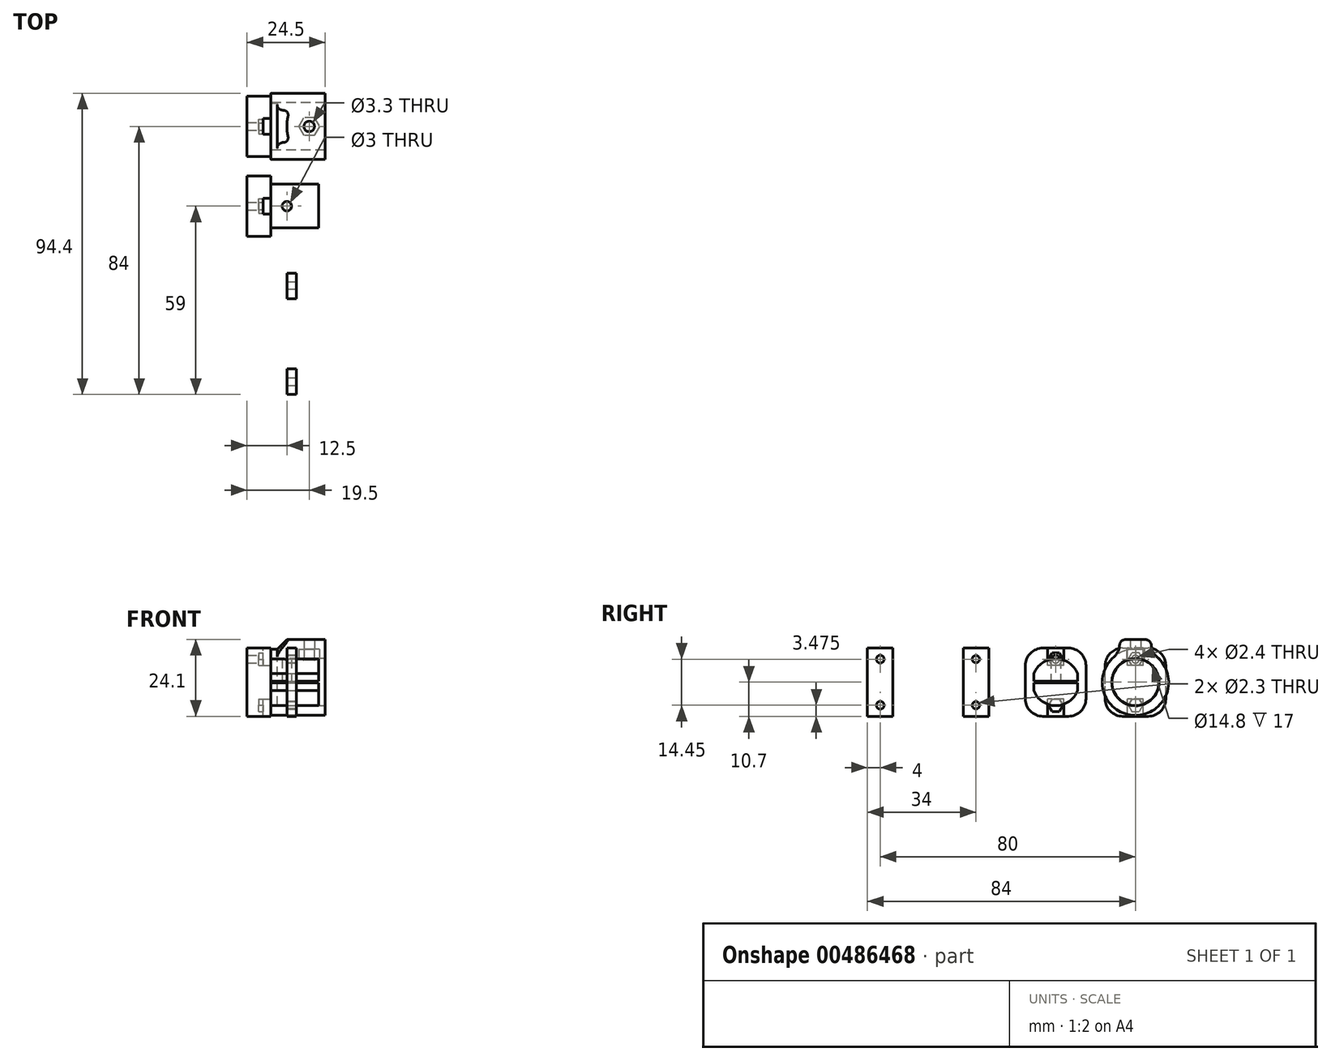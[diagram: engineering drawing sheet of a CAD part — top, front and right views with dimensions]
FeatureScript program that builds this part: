
annotation { "Feature Type Name" : "Feature", "Feature Type Description" : "" }
export const myFeature = defineFeature(function(context is Context, id is Id, definition is map)
    precondition{}
    {
        {
            assignVariable(context, id + "F0", {"name" : "nut_distance", "anyValue" : 5 * mm});
        }
        {
            var Q0;
            Q0=qCreatedBy(makeId("Front.planeOp"),FACE);
            var sketch = newSketch(context, id + "F1", { "sketchPlane" : qUnion([Q0])});
            skLineSegment(sketch, "E0", {"start": v(0, 3.75) * mm, "end": v(-7.5, 3.75) * mm});
            skLineSegment(sketch, "E1", {"start": v(-7.5, -3.75) * mm, "end": v(-7.5, 3.75) * mm});
            skLineSegment(sketch, "E2", {"start": v(-7.5, -3.75) * mm, "end": v(0, -3.75) * mm});
            skLineSegment(sketch, "E3", {"start": v(0, -10.7) * mm, "end": v(0, -3.75) * mm});
            skLineSegment(sketch, "E4", {"start": v(0, -10.7) * mm, "end": v(-12.5, -10.7) * mm});
            skLineSegment(sketch, "E5", {"start": v(-12.5, -10.7) * mm, "end": v(-12.5, 10.7) * mm});
            skLineSegment(sketch, "E6", {"start": v(0, 3.75) * mm, "end": v(0, 10.7) * mm});
            skLineSegment(sketch, "E7", {"start": v(-12.5, 10.7) * mm, "end": v(0, 10.7) * mm});
            skSolve(sketch);
        }
        {
            var Q0;
            Q0=qSketchRegion(id+"F1",true);
            extrude(context, id + "F2", {"entities" : qUnion([Q0]), "depth" : 8 * mm, "offsetDistance" : 25 * mm, "symmetric" : true});
        }
        {
            var Q0;
            Q0=makeQuery(id+"F2.opExtrude","SWEPT_FACE",FACE,{"disambiguationData":[OSD([sQuery(id+"F1.wireOp",EDGE,"E6")])]});
            var sketch = newSketch(context, id + "F3", { "sketchPlane" : qUnion([Q0])});
            skLineSegment(sketch, "E8", {"start": v(-12.42, 0) * mm, "end": v(17.97, 0) * mm, "construction": true});
            skLineSegment(sketch, "E9", {"start": v(0, 22.03) * mm, "end": v(0, -15.29) * mm, "construction": true});
            skPoint(sketch, "E9.startSnap0", {"position": v(0, 10.7) * mm});
            skLineSegment(sketch, "E10", {"start": v(0, 5.25) * mm, "end": v(-1.14, 5.25) * mm});
            skLineSegment(sketch, "E11", {"start": v(-1.14, 5.25) * mm, "end": v(-2.28, 7.22) * mm});
            skLineSegment(sketch, "E12", {"start": v(-2.28, 7.22) * mm, "end": v(0, 7.22) * mm, "construction": true});
            skLineSegment(sketch, "E13", {"start": v(0, 7.22) * mm, "end": v(1.14, 5.25) * mm, "construction": true});
            skLineSegment(sketch, "E14.MirrorCS", {"start": v(-1.14, 9.2) * mm, "end": v(-2.28, 7.22) * mm});
            skLineSegment(sketch, "E15.MirrorCS", {"start": v(0, 9.2) * mm, "end": v(-1.14, 9.2) * mm});
            skLineSegment(sketch, "E16.MirrorCS", {"start": v(0, 9.2) * mm, "end": v(1.14, 9.2) * mm});
            skLineSegment(sketch, "E17.MirrorCS", {"start": v(1.14, 9.2) * mm, "end": v(2.28, 7.23) * mm});
            skLineSegment(sketch, "E18.MirrorCS", {"start": v(1.14, 5.25) * mm, "end": v(2.28, 7.23) * mm});
            skLineSegment(sketch, "E19.MirrorCS", {"start": v(0, 5.25) * mm, "end": v(1.14, 5.25) * mm});
            skLineSegment(sketch, "E20.MirrorCS", {"start": v(-1.14, -9.2) * mm, "end": v(-2.28, -7.22) * mm});
            skLineSegment(sketch, "E21.MirrorCS", {"start": v(0, -9.2) * mm, "end": v(-1.14, -9.2) * mm});
            skLineSegment(sketch, "E22.MirrorCS", {"start": v(0, -9.2) * mm, "end": v(1.14, -9.2) * mm});
            skLineSegment(sketch, "E23.MirrorCS", {"start": v(1.14, -9.2) * mm, "end": v(2.28, -7.23) * mm});
            skLineSegment(sketch, "E24.MirrorCS", {"start": v(1.14, -5.25) * mm, "end": v(2.28, -7.23) * mm});
            skLineSegment(sketch, "E25.MirrorCS", {"start": v(0, -5.25) * mm, "end": v(1.14, -5.25) * mm});
            skLineSegment(sketch, "E26.MirrorCS", {"start": v(0, -5.25) * mm, "end": v(-1.14, -5.25) * mm});
            skLineSegment(sketch, "E27.MirrorCS", {"start": v(-1.14, -5.25) * mm, "end": v(-2.28, -7.23) * mm});
            skSolve(sketch);
        }
        {
            var Q0;
            Q0=makeQuery(id+"F3.imprint","IMPRINT",FACE,{"disambiguationData":[TD([[makeQuery(id+"F3.imprint","IMPRINT",EDGE,{"derivedFrom":sQuery(id+"F3.wireOp",EDGE,"E10")}),-1.0]])]});
            var Q1;
            Q1=makeQuery(id+"F3.imprint","IMPRINT",FACE,{"disambiguationData":[TD([[makeQuery(id+"F3.imprint","IMPRINT",EDGE,{"derivedFrom":sQuery(id+"F3.wireOp",EDGE,"E20.MirrorCS")}),-1.0]])]});
            extrude(context, id + "F4", {"entities" : qUnion([Q0, Q1]), "operationType" : NewBodyOperationType.REMOVE, "oppositeDirection" : true, "depth" : 5.4 * mm, "hasOffset" : true, "offsetDistance" : 4 * mm, "hasSecondDirection" : true, "secondDirectionOppositeDirection" : true, "secondDirectionDepth" : getVariable(context, 'nut_distance') - 1.3 * mm});
        }
        {
            var Q0;
            Q0=makeQuery(id+"F2.opExtrude","SWEPT_FACE",FACE,{"disambiguationData":[OSD([sQuery(id+"F1.wireOp",EDGE,"E7")])]});
            var sketch = newSketch(context, id + "F5", { "sketchPlane" : qUnion([Q0])});
            skLineSegment(sketch, "E28.bottom", {"start": v(-7.5, 2.5) * mm, "end": v(-5, 2.5) * mm});
            skLineSegment(sketch, "E28.top", {"start": v(-7.5, -2.5) * mm, "end": v(-5, -2.5) * mm});
            skLineSegment(sketch, "E28.left", {"start": v(-7.5, 2.5) * mm, "end": v(-7.5, -2.5) * mm});
            skLineSegment(sketch, "E28.right", {"start": v(-5, 2.5) * mm, "end": v(-5, -2.5) * mm});
            skSolve(sketch);
        }
        {
            var Q0;
            Q0=qSketchRegion(id+"F5",true);
            var Q1;
            Q1=makeQuery(id+"F4.boolean.opBoolean","COPY",VERTEX,{"derivedFrom":makeQuery(id+"F4.opExtrude","CAP_VERTEX",VERTEX,{"disambiguationData":[OSD([sQuery(id+"F3.wireOp",EDGE,"E10"),sQuery(id+"F3.wireOp",EDGE,"E11")])],"isStart":false})});
            extrude(context, id + "F6", {"entities" : qUnion([Q0]), "operationType" : NewBodyOperationType.REMOVE, "endBound" : BoundingType.UP_TO_VERTEX, "oppositeDirection" : true, "depth" : 25 * mm, "endBoundEntityVertex" : qUnion([Q1]), "offsetDistance" : 25 * mm});
        }
        {
            var Q0;
            Q0=makeQuery(id+"F2.opExtrude","SWEPT_FACE",FACE,{"disambiguationData":[OSD([sQuery(id+"F1.wireOp",EDGE,"E6")])]});
            var sketch = newSketch(context, id + "F7", { "sketchPlane" : qUnion([Q0])});
            skCircle(sketch, "E29", {"center": v(0, 7.22) * mm, "radius": 1.2 * mm});
            skCircle(sketch, "E30.MirrorC", {"center": v(0, -7.22) * mm, "radius": 1.2 * mm});
            skSolve(sketch);
        }
        {
            var Q0;
            Q0=makeQuery(id+"F7.imprint","IMPRINT",FACE,{"disambiguationData":[TD([[makeQuery(id+"F7.imprint","IMPRINT",EDGE,{"derivedFrom":sQuery(id+"F7.wireOp",EDGE,"E29")}),1.0]])]});
            var Q1;
            Q1=makeQuery(id+"F7.imprint","IMPRINT",FACE,{"disambiguationData":[TD([[makeQuery(id+"F7.imprint","IMPRINT",EDGE,{"derivedFrom":sQuery(id+"F7.wireOp",EDGE,"E30.MirrorC")}),-1.0]])]});
            var Q2;
            Q2=makeQuery(id+"F4.boolean.opBoolean","COPY",VERTEX,{"derivedFrom":makeQuery(id+"F4.opExtrude","CAP_VERTEX",VERTEX,{"disambiguationData":[OSD([sQuery(id+"F3.wireOp",EDGE,"E17.MirrorCS"),sQuery(id+"F3.wireOp",EDGE,"E18.MirrorCS")])],"isStart":false})});
            extrude(context, id + "F8", {"entities" : qUnion([Q0, Q1]), "operationType" : NewBodyOperationType.REMOVE, "endBound" : BoundingType.THROUGH_ALL, "oppositeDirection" : true, "depth" : 25 * mm, "endBoundEntityVertex" : qUnion([Q2]), "offsetDistance" : 25 * mm});
        }
        {
            var Q0;
            Q0=qSketchRegion(id+"F5",true);
            var Q1;
            Q1=makeQuery(id+"F2.opExtrude","SWEPT_FACE",FACE,{"disambiguationData":[OSD([sQuery(id+"F1.wireOp",EDGE,"E4")])]});
            var Q2;
            Q2=makeQuery(id+"F4.boolean.opBoolean","COPY",VERTEX,{"derivedFrom":makeQuery(id+"F4.opExtrude","CAP_VERTEX",VERTEX,{"disambiguationData":[OSD([sQuery(id+"F3.wireOp",EDGE,"E26.MirrorCS"),sQuery(id+"F3.wireOp",EDGE,"E27.MirrorCS")])],"isStart":false})});
            extrude(context, id + "F9", {"entities" : qUnion([Q0]), "operationType" : NewBodyOperationType.REMOVE, "endBound" : BoundingType.UP_TO_SURFACE, "oppositeDirection" : true, "depth" : 25 * mm, "endBoundEntityFace" : qUnion([Q1]), "offsetDistance" : 25 * mm, "hasSecondDirection" : true, "secondDirectionBound" : BoundingType.UP_TO_VERTEX, "secondDirectionOppositeDirection" : true, "secondDirectionDepth" : 25 * mm, "secondDirectionBoundEntityVertex" : qUnion([Q2])});
        }
        {
            var Q0;
            Q0=qSketchRegion(id+"F3",true);
            extrude(context, id + "F10", {"entities" : qUnion([Q0]), "operationType" : NewBodyOperationType.REMOVE, "oppositeDirection" : true, "depth" : (7.5 + 1.3) * mm, "offsetDistance" : 25 * mm, "hasSecondDirection" : true, "secondDirectionOppositeDirection" : true, "secondDirectionDepth" : (5.4 + 1.7) * mm});
        }
        {
            var Q0;
            Q0=qCreatedBy(makeId("Front.planeOp"),FACE);
            cPlane(context, id + "F11", {"entities" : qUnion([Q0]), "cplaneType" : CPlaneType.OFFSET, "offset" : 25 * mm, "width" : 150 * mm, "height" : 150 * mm});
        }
        {
            var Q0;
            Q0=qCreatedBy(makeId("Right.planeOp"),FACE);
            var sketch = newSketch(context, id + "F12", { "sketchPlane" : qUnion([Q0])});
            skLineSegment(sketch, "E31.bottom", {"start": v(-21, 10.7) * mm, "end": v(-29, 10.7) * mm});
            skLineSegment(sketch, "E31.top", {"start": v(-21, -10.7) * mm, "end": v(-29, -10.7) * mm});
            skLineSegment(sketch, "E31.left", {"start": v(-21, 10.7) * mm, "end": v(-21, -10.7) * mm});
            skLineSegment(sketch, "E31.right", {"start": v(-29, 10.7) * mm, "end": v(-29, -10.7) * mm});
            skCircle(sketch, "E32", {"center": v(-25, 7.22) * mm, "radius": 1.15 * mm});
            skCircle(sketch, "E33.MirrorC", {"center": v(-25, -7.22) * mm, "radius": 1.15 * mm});
            skSolve(sketch);
        }
        {
            var Q0;
            Q0=makeQuery(id+"F12.imprint","IMPRINT",FACE,{"disambiguationData":[TD([[makeQuery(id+"F12.imprint","IMPRINT",EDGE,{"derivedFrom":sQuery(id+"F12.wireOp",EDGE,"E31.bottom")}),1.0]])]});
            extrude(context, id + "F13", {"entities" : qUnion([Q0]), "depth" : 3 * mm, "offsetDistance" : 25 * mm});
        }
        {
            var Q0;
            Q0=qCreatedBy(id+"F11.planeOp",FACE);
            var sketch = newSketch(context, id + "F14", { "sketchPlane" : qUnion([Q0])});
            skArc(sketch, "E34", {"start": v(0, 3.75) * mm, "mid": v(-0.1, 0) * mm, "end": v(0, -3.75) * mm});
            skLineSegment(sketch, "E35", {"start": v(0, 3.75) * mm, "end": v(0, -3.75) * mm});
            skSolve(sketch);
        }
        {
            var Q0;
            Q0=makeQuery(id+"F13.opExtrude","SWEPT_BODY",BODY,{"disambiguationData":[OSD([sQuery(id+"F12.wireOp",EDGE,"E31.bottom"),sQuery(id+"F12.wireOp",EDGE,"E31.top"),sQuery(id+"F12.wireOp",EDGE,"E31.left"),sQuery(id+"F12.wireOp",EDGE,"E31.right"),sQuery(id+"F12.wireOp",EDGE,"E32"),sQuery(id+"F12.wireOp",EDGE,"E33.MirrorC")])]});
            transform(context, id + "F15", {"entities" : qUnion([Q0]), "transformType" : TransformType.TRANSLATION_3D, "dx" : 0 * mm, "dy" : -30 * mm, "dz" : 0 * mm, "makeCopy" : true});
        }
        {
            var Q0;
            Q0=makeQuery(id+"F15.opPattern","COPY",FACE,{"derivedFrom":makeQuery(id+"F13.opExtrude","CAP_FACE",FACE,{"disambiguationData":[OSD([sQuery(id+"F12.wireOp",EDGE,"E31.bottom"),sQuery(id+"F12.wireOp",EDGE,"E31.top"),sQuery(id+"F12.wireOp",EDGE,"E31.left"),sQuery(id+"F12.wireOp",EDGE,"E31.right"),sQuery(id+"F12.wireOp",EDGE,"E32"),sQuery(id+"F12.wireOp",EDGE,"E33.MirrorC")])],"isStart":false}),"instanceName":"1"});
            var sketch = newSketch(context, id + "F16", { "sketchPlane" : qUnion([Q0])});
            skCircle(sketch, "E36", {"center": v(-55, 7.22) * mm, "radius": 1.2 * mm});
            skCircle(sketch, "E37.MirrorC", {"center": v(-55, -7.22) * mm, "radius": 1.2 * mm});
            skSolve(sketch);
        }
        {
            var Q0;
            Q0=qSketchRegion(id+"F16",true);
            extrude(context, id + "F17", {"entities" : qUnion([Q0]), "operationType" : NewBodyOperationType.REMOVE, "endBound" : BoundingType.THROUGH_ALL, "oppositeDirection" : true, "depth" : 25 * mm, "offsetDistance" : 25 * mm});
        }
        {
            var Q0;
            Q0=qCreatedBy(makeId("Right.planeOp"),FACE);
            var sketch = newSketch(context, id + "F18", { "sketchPlane" : qUnion([Q0])});
            skCircle(sketch, "E38", {"center": v(0, 0) * mm, "radius": 7.35 * mm});
            skSolve(sketch);
        }
        {
            var Q0;
            Q0=makeQuery(id+"F2.opExtrude","SWEPT_FACE",FACE,{"disambiguationData":[OSD([sQuery(id+"F1.wireOp",EDGE,"E1")])]});
            var sketch = newSketch(context, id + "F19", { "sketchPlane" : qUnion([Q0])});
            skLineSegment(sketch, "E39.bottom", {"start": v(4, 3.75) * mm, "end": v(-4, 3.75) * mm});
            skLineSegment(sketch, "E39.top", {"start": v(4, -3.75) * mm, "end": v(-4, -3.75) * mm});
            skLineSegment(sketch, "E39.left", {"start": v(4, 3.75) * mm, "end": v(4, -3.75) * mm});
            skLineSegment(sketch, "E39.right", {"start": v(-4, 3.75) * mm, "end": v(-4, -3.75) * mm});
            skSolve(sketch);
        }
        {
            var Q0;
            Q0 = qSketchRegion(id + "F19", true);
            var Q1;
            Q1=makeQuery(id+"F2.opExtrude","SWEPT_FACE",FACE,{"disambiguationData":[OSD([sQuery(id+"F1.wireOp",EDGE,"E6")])]});
            extrude(context, id + "F20", {"entities" : qUnion([Q0]), "operationType" : NewBodyOperationType.ADD, "endBound" : BoundingType.UP_TO_SURFACE, "depth" : 25 * mm, "endBoundEntityFace" : qUnion([Q1]), "offsetDistance" : 25 * mm});
        }
        {
            var Q0;
            Q0 = qSketchRegion(id + "F18", true);
            extrude(context, id + "F21", {"entities" : qUnion([Q0]), "operationType" : NewBodyOperationType.ADD, "oppositeDirection" : true, "depth" : 5 * mm, "offsetDistance" : 25 * mm, "hasSecondDirection" : true, "secondDirectionOppositeDirection" : false, "secondDirectionDepth" : 10 * mm});
        }
        {
            var Q0;
            {var subQ0=sQuery(id+"F1.wireOp",EDGE,"E7");var subQ1=sQuery(id+"F1.wireOp",EDGE,"E6");var subQ4=sQuery(id+"F1.wireOp",EDGE,"E3");var subQ8=makeQuery(id+"F2.opExtrude","SWEPT_FACE",FACE,{"disambiguationData":[OSD([subQ1])]});var subQ9=sQuery(id+"F19.wireOp",EDGE,"E39.left");var subQ10=sQuery(id+"F19.wireOp",EDGE,"E39.right");Q0=makeQuery(id+"F21.boolean.opBoolean","SPLIT",FACE,{"disambiguationData":[TD([makeQuery(id+"F2.opExtrude","SWEPT_FACE",FACE,{"disambiguationData":[OSD([subQ0])]})])],"derivedFrom":makeQuery(id+"F20.boolean.opBoolean","MERGE",FACE,{"derivedFrom":[makeQuery(id+"F2.opExtrude","SWEPT_FACE",FACE,{"disambiguationData":[OSD([subQ4])]}),subQ8,makeQuery(id+"F20.opExtrude","CAP_FACE",FACE,{"disambiguationData":[OSD([sQuery(id+"F19.wireOp",EDGE,"E39.bottom"),sQuery(id+"F19.wireOp",EDGE,"E39.top"),subQ9,subQ10])],"isStart":false})]})});}
            var sketch = newSketch(context, id + "F22", { "sketchPlane" : qUnion([Q0])});
            skArc(sketch, "E40", {"start": v(4, 6.17) * mm, "mid": v(0, 7.35) * mm, "end": v(-4, 6.17) * mm});
            skLineSegment(sketch, "E41", {"start": v(-4, 6.17) * mm, "end": v(-4, 10.7) * mm});
            skLineSegment(sketch, "E42", {"start": v(-4, 10.7) * mm, "end": v(4, 10.7) * mm});
            skLineSegment(sketch, "E43", {"start": v(4, 10.7) * mm, "end": v(4, 6.17) * mm});
            skArc(sketch, "E44.MirrorCS", {"start": v(4, -6.17) * mm, "mid": v(0, -7.35) * mm, "end": v(-4, -6.17) * mm});
            skLineSegment(sketch, "E45.MirrorCS", {"start": v(-4, -10.7) * mm, "end": v(4, -10.7) * mm});
            skLineSegment(sketch, "E46.MirrorCS", {"start": v(-4, -6.17) * mm, "end": v(-4, -10.7) * mm});
            skLineSegment(sketch, "E47.MirrorCS", {"start": v(4, -10.7) * mm, "end": v(4, -6.17) * mm});
            skSolve(sketch);
        }
        {
            var Q0;
            Q0 = qSketchRegion(id + "F22", true);
            extrude(context, id + "F23", {"entities" : qUnion([Q0]), "operationType" : NewBodyOperationType.REMOVE, "oppositeDirection" : true, "depth" : 5 * mm, "offsetDistance" : 25 * mm});
        }
        {
            var Q0;
            Q0=makeQuery(id+"F2.opExtrude","SWEPT_FACE",FACE,{"disambiguationData":[OSD([sQuery(id+"F1.wireOp",EDGE,"E5")])]});
            var sketch = newSketch(context, id + "F24", { "sketchPlane" : qUnion([Q0])});
            skPoint(sketch, "E48", {"position": v(4, -10.7) * mm});
            skPoint(sketch, "E49", {"position": v(4, 10.7) * mm});
            skLineSegment(sketch, "E50.bottom", {"start": v(9.5, -10.7) * mm, "end": v(4, -10.7) * mm});
            skLineSegment(sketch, "E50.top", {"start": v(9.5, 10.7) * mm, "end": v(4, 10.7) * mm});
            skLineSegment(sketch, "E50.left", {"start": v(9.5, -10.7) * mm, "end": v(9.5, 10.7) * mm});
            skLineSegment(sketch, "E50.right", {"start": v(4, -10.7) * mm, "end": v(4, 10.7) * mm});
            skPoint(sketch, "E51.MirrorP", {"position": v(-4, 10.7) * mm});
            skPoint(sketch, "E52.MirrorP", {"position": v(-4, -10.7) * mm});
            skLineSegment(sketch, "E53.MirrorCS", {"start": v(-9.5, -10.7) * mm, "end": v(-4, -10.7) * mm});
            skLineSegment(sketch, "E54.MirrorCS", {"start": v(-4, -10.7) * mm, "end": v(-4, 10.7) * mm});
            skLineSegment(sketch, "E55.MirrorCS", {"start": v(-9.5, -10.7) * mm, "end": v(-9.5, 10.7) * mm});
            skLineSegment(sketch, "E56.MirrorCS", {"start": v(-9.5, 10.7) * mm, "end": v(-4, 10.7) * mm});
            skSolve(sketch);
        }
        {
            var Q0;
            Q0 = qSketchRegion(id + "F24", true);
            var Q1;
            {var subQ0=sQuery(id+"F18.wireOp",EDGE,"E38");Q1=makeQuery(id+"F21.boolean.opBoolean","SPLIT",FACE,{"disambiguationData":[TD([makeQuery(id+"F20.opExtrude","SWEPT_FACE",FACE,{"disambiguationData":[OSD([sQuery(id+"F19.wireOp",EDGE,"E39.right")])]})])],"derivedFrom":makeQuery(id+"F21.opExtrude","CAP_FACE",FACE,{"disambiguationData":[OSD([subQ0])],"isStart":false})});}
            extrude(context, id + "F25", {"entities" : qUnion([Q0]), "operationType" : NewBodyOperationType.ADD, "endBound" : BoundingType.UP_TO_SURFACE, "oppositeDirection" : true, "depth" : 5 * mm, "endBoundEntityFace" : qUnion([Q1]), "offsetDistance" : 25 * mm});
        }
        {
            var Q0;
            Q0=makeQuery(id+"F25.opExtrude","SWEPT_EDGE",EDGE,{"disambiguationData":[OSD([sQuery(id+"F24.wireOp",EDGE,"E50.top"),sQuery(id+"F24.wireOp",EDGE,"E50.left")])]});
            var Q1;
            Q1=makeQuery(id+"F25.opExtrude","SWEPT_EDGE",EDGE,{"disambiguationData":[OSD([sQuery(id+"F24.wireOp",EDGE,"E55.MirrorCS"),sQuery(id+"F24.wireOp",EDGE,"E56.MirrorCS")])]});
            var Q2;
            Q2=makeQuery(id+"F25.opExtrude","SWEPT_EDGE",EDGE,{"disambiguationData":[OSD([sQuery(id+"F24.wireOp",EDGE,"E53.MirrorCS"),sQuery(id+"F24.wireOp",EDGE,"E55.MirrorCS")])]});
            var Q3;
            Q3=makeQuery(id+"F25.opExtrude","SWEPT_EDGE",EDGE,{"disambiguationData":[OSD([sQuery(id+"F24.wireOp",EDGE,"E50.bottom"),sQuery(id+"F24.wireOp",EDGE,"E50.left")])]});
            fillet(context, id + "F26", {"entities" : qUnion([Q0, Q1, Q2, Q3]), "radius" : 5.5 * mm, "tangentPropagation" : true, "allowEdgeOverflow" : false});
        }
        {
            var Q0;
            Q0=qCreatedBy(makeId("Top.planeOp"),FACE);
            var sketch = newSketch(context, id + "F27", { "sketchPlane" : qUnion([Q0])});
            skCircle(sketch, "E57", {"center": v(0, 0) * mm, "radius": 1.5 * mm});
            skSolve(sketch);
        }
        {
            var Q0;
            Q0 = qSketchRegion(id + "F27", true);
            extrude(context, id + "F28", {"entities" : qUnion([Q0]), "operationType" : NewBodyOperationType.REMOVE, "depth" : 25 * mm, "offsetDistance" : 25 * mm, "hasSecondDirection" : true, "secondDirectionOppositeDirection" : false, "secondDirectionDepth" : 0 * mm});
        }
        {
            var Q0;
            Q0=qCreatedBy(makeId("Front.planeOp"),FACE);
            cPlane(context, id + "F29", {"entities" : qUnion([Q0]), "cplaneType" : CPlaneType.OFFSET, "offset" : 25 * mm, "oppositeDirection" : true, "width" : 150 * mm, "height" : 150 * mm});
        }
        {
            var Q0;
            Q0=makeQuery(id+"F2.opExtrude","SWEPT_BODY",BODY,{"disambiguationData":[OSD([sQuery(id+"F1.wireOp",EDGE,"E0"),sQuery(id+"F1.wireOp",EDGE,"E1"),sQuery(id+"F1.wireOp",EDGE,"E2"),sQuery(id+"F1.wireOp",EDGE,"E3"),sQuery(id+"F1.wireOp",EDGE,"E4"),sQuery(id+"F1.wireOp",EDGE,"E5"),sQuery(id+"F1.wireOp",EDGE,"E6"),sQuery(id+"F1.wireOp",EDGE,"E7")])]});
            transform(context, id + "F30", {"entities" : qUnion([Q0]), "transformType" : TransformType.TRANSLATION_3D, "dx" : 0 * mm, "dy" : 25 * mm, "dz" : 0 * mm, "makeCopy" : true});
        }
        {
            var Q0;
            Q0=qCreatedBy(makeId("Right.planeOp"),FACE);
            var sketch = newSketch(context, id + "F31", { "sketchPlane" : qUnion([Q0])});
            skCircle(sketch, "E58", {"center": v(25, 0) * mm, "radius": 7.35 * mm});
            skSolve(sketch);
        }
        {
            var Q0;
            Q0=qCreatedBy(makeId("Right.planeOp"),FACE);
            var sketch = newSketch(context, id + "F32", { "sketchPlane" : qUnion([Q0])});
            skCircle(sketch, "E59", {"center": v(25, 0) * mm, "radius": 7.4 * mm});
            skCircle(sketch, "E60", {"center": v(25, 0) * mm, "radius": 10.4 * mm});
            skSolve(sketch);
        }
        {
            var Q0;
            Q0 = qSketchRegion(id + "F32", true);
            extrude(context, id + "F33", {"entities" : qUnion([Q0]), "operationType" : NewBodyOperationType.ADD, "depth" : 12 * mm, "offsetDistance" : 25 * mm, "hasSecondDirection" : true, "secondDirectionOppositeDirection" : true, "secondDirectionDepth" : 5 * mm});
        }
        {
            var Q0;
            Q0 = qSketchRegion(id + "F31", true);
            extrude(context, id + "F34", {"entities" : qUnion([Q0]), "operationType" : NewBodyOperationType.REMOVE, "oppositeDirection" : true, "depth" : 3 * mm, "offsetDistance" : 25 * mm, "hasSecondDirection" : true, "secondDirectionOppositeDirection" : false, "secondDirectionDepth" : 10 * mm});
        }
        {
            var Q0;
            Q0=qCreatedBy(makeId("Top.planeOp"),FACE);
            cPlane(context, id + "F35", {"entities" : qUnion([Q0]), "cplaneType" : CPlaneType.OFFSET, "offset" : (14.8 / 2) * mm, "width" : 150 * mm, "height" : 150 * mm});
        }
        {
            var Q0;
            Q0=qCreatedBy(id+"F35.planeOp",FACE);
            var sketch = newSketch(context, id + "F36", { "sketchPlane" : qUnion([Q0])});
            skCircle(sketch, "E61.cCircle", {"center": v(7, 25) * mm, "radius": 2.8 * mm, "construction": true});
            skLineSegment(sketch, "E61.0", {"start": v(5.38, 27.8) * mm, "end": v(8.62, 27.8) * mm});
            skLineSegment(sketch, "E61.1", {"start": v(8.62, 27.8) * mm, "end": v(10.23, 25) * mm});
            skLineSegment(sketch, "E61.2", {"start": v(10.23, 25) * mm, "end": v(8.62, 22.2) * mm});
            skLineSegment(sketch, "E61.3", {"start": v(8.62, 22.2) * mm, "end": v(5.38, 22.2) * mm});
            skLineSegment(sketch, "E61.4", {"start": v(5.38, 22.2) * mm, "end": v(3.77, 25) * mm});
            skLineSegment(sketch, "E61.5", {"start": v(3.77, 25) * mm, "end": v(5.38, 27.8) * mm});
            skPoint(sketch, "E61.0.midPoint", {"position": v(7, 27.8) * mm});
            skSolve(sketch);
        }
        {
            var Q0;
            Q0=makeQuery(id+"F36.imprint","IMPRINT",FACE,{"disambiguationData":[TD([[makeQuery(id+"F36.imprint","IMPRINT",EDGE,{"derivedFrom":sQuery(id+"F36.wireOp",EDGE,"E61.0")}),-1.0]])]});
            var sketch = newSketch(context, id + "F37", { "sketchPlane" : qUnion([Q0])});
            skLineSegment(sketch, "E62.bottom", {"start": v(12, 20) * mm, "end": v(2, 20) * mm});
            skLineSegment(sketch, "E62.top", {"start": v(12, 30) * mm, "end": v(2, 30) * mm});
            skLineSegment(sketch, "E62.left", {"start": v(12, 20) * mm, "end": v(12, 30) * mm});
            skLineSegment(sketch, "E62.right", {"start": v(2, 20) * mm, "end": v(2, 30) * mm});
            skSolve(sketch);
        }
        {
            var Q0;
            Q0 = qSketchRegion(id + "F37", true);
            extrude(context, id + "F38", {"entities" : qUnion([Q0]), "operationType" : NewBodyOperationType.ADD, "depth" : 6 * mm, "offsetDistance" : 25 * mm});
        }
        {
            var Q0;
            Q0 = qSketchRegion(id + "F36", true);
            extrude(context, id + "F39", {"entities" : qUnion([Q0]), "operationType" : NewBodyOperationType.REMOVE, "depth" : 3 * mm, "offsetDistance" : 25 * mm, "hasSecondDirection" : true, "secondDirectionOppositeDirection" : true, "secondDirectionDepth" : 5 * mm});
        }
        {
            var Q0;
            Q0=qCreatedBy(id+"F35.planeOp",FACE);
            var sketch = newSketch(context, id + "F40", { "sketchPlane" : qUnion([Q0])});
            skCircle(sketch, "E63", {"center": v(7, 25) * mm, "radius": 1.65 * mm});
            skSolve(sketch);
        }
        {
            var Q0;
            Q0 = qSketchRegion(id + "F40", true);
            var Q1;
            Q1=makeQuery(id+"F38.opExtrude","CAP_FACE",FACE,{"disambiguationData":[OSD([sQuery(id+"F37.wireOp",EDGE,"E62.bottom"),sQuery(id+"F37.wireOp",EDGE,"E62.top"),sQuery(id+"F37.wireOp",EDGE,"E62.left"),sQuery(id+"F37.wireOp",EDGE,"E62.right")])],"isStart":false});
            extrude(context, id + "F41", {"entities" : qUnion([Q0]), "operationType" : NewBodyOperationType.REMOVE, "endBound" : BoundingType.UP_TO_SURFACE, "depth" : 25 * mm, "endBoundEntityFace" : qUnion([Q1]), "offsetDistance" : 25 * mm});
        }
        {
            var Q0;
            Q0=makeQuery(id+"F38.boolean.opBoolean","INTERSECT",EDGE,{"derivedFrom":[makeQuery(id+"F33.opExtrude","SWEPT_FACE",FACE,{"disambiguationData":[OSD([sQuery(id+"F32.wireOp",EDGE,"E60")])]}),makeQuery(id+"F38.opExtrude","SWEPT_FACE",FACE,{"disambiguationData":[OSD([sQuery(id+"F37.wireOp",EDGE,"E62.right")])]})]});
            chamfer(context, id + "F42", {"entities" : qUnion([Q0]), "chamferType" : ChamferType.OFFSET_ANGLE, "width" : 5 * mm, "oppositeDirection" : false, "angle" : 45 * degree, "tangentPropagation" : true});
        }
        {
            var Q0;
            Q0=makeQuery(id+"F38.opExtrude","CAP_EDGE",EDGE,{"disambiguationData":[OSD([sQuery(id+"F37.wireOp",EDGE,"E62.top")])],"isStart":false});
            var Q1;
            Q1=makeQuery(id+"F38.opExtrude","CAP_EDGE",EDGE,{"disambiguationData":[OSD([sQuery(id+"F37.wireOp",EDGE,"E62.bottom")])],"isStart":false});
            fillet(context, id + "F43", {"entities" : qUnion([Q0, Q1]), "radius" : 2 * mm, "tangentPropagation" : true, "allowEdgeOverflow" : false});
        }
        {
            var Q0;
            Q0=makeQuery(id+"F38.boolean.opBoolean","INTERSECT",EDGE,{"derivedFrom":[makeQuery(id+"F33.opExtrude","SWEPT_FACE",FACE,{"disambiguationData":[OSD([sQuery(id+"F32.wireOp",EDGE,"E60")])]}),makeQuery(id+"F38.opExtrude","SWEPT_FACE",FACE,{"disambiguationData":[OSD([sQuery(id+"F37.wireOp",EDGE,"E62.top")])]})]});
            var Q1;
            Q1=makeQuery(id+"F38.boolean.opBoolean","INTERSECT",EDGE,{"derivedFrom":[makeQuery(id+"F33.opExtrude","SWEPT_FACE",FACE,{"disambiguationData":[OSD([sQuery(id+"F32.wireOp",EDGE,"E60")])]}),makeQuery(id+"F38.opExtrude","SWEPT_FACE",FACE,{"disambiguationData":[OSD([sQuery(id+"F37.wireOp",EDGE,"E62.bottom")])]})]});
            fillet(context, id + "F44", {"entities" : qUnion([Q0, Q1]), "radius" : 5 * mm, "tangentPropagation" : true, "allowEdgeOverflow" : false});
        }
        {
            var Q0;
            Q0=makeQuery(id+"F21.opExtrude","CAP_FACE",FACE,{"disambiguationData":[OSD([sQuery(id+"F18.wireOp",EDGE,"E38")])],"isStart":true});
            var sketch = newSketch(context, id + "F45", { "sketchPlane" : qUnion([Q0])});
            skLineSegment(sketch, "E64.bottom", {"start": v(-9.5, 0.25) * mm, "end": v(9.5, 0.25) * mm});
            skLineSegment(sketch, "E64.top", {"start": v(-9.5, -0.25) * mm, "end": v(9.5, -0.25) * mm});
            skLineSegment(sketch, "E64.left", {"start": v(-9.5, 0.25) * mm, "end": v(-9.5, -0.25) * mm});
            skLineSegment(sketch, "E64.right", {"start": v(9.5, 0.25) * mm, "end": v(9.5, -0.25) * mm});
            skLineSegment(sketch, "E65", {"start": v(6.85, 0.25) * mm, "end": v(6.85, 2.66) * mm});
            skLineSegment(sketch, "E66", {"start": v(6.85, 2.66) * mm, "end": v(9.5, 2.66) * mm});
            skLineSegment(sketch, "E67", {"start": v(9.5, 2.66) * mm, "end": v(9.5, 0.25) * mm});
            skLineSegment(sketch, "E68.MirrorCS", {"start": v(6.85, -2.66) * mm, "end": v(9.5, -2.66) * mm});
            skLineSegment(sketch, "E69.MirrorCS", {"start": v(9.5, -2.66) * mm, "end": v(9.5, -0.25) * mm});
            skLineSegment(sketch, "E70.MirrorCS", {"start": v(6.85, -0.25) * mm, "end": v(6.85, -2.66) * mm});
            skLineSegment(sketch, "E71.MirrorCS", {"start": v(-6.85, 0.25) * mm, "end": v(-6.85, 2.66) * mm});
            skLineSegment(sketch, "E72.MirrorCS", {"start": v(-6.85, 2.66) * mm, "end": v(-9.5, 2.66) * mm});
            skLineSegment(sketch, "E73.MirrorCS", {"start": v(-9.5, 2.66) * mm, "end": v(-9.5, 0.25) * mm});
            skLineSegment(sketch, "E74.MirrorCS", {"start": v(-9.5, -2.66) * mm, "end": v(-9.5, -0.25) * mm});
            skLineSegment(sketch, "E75.MirrorCS", {"start": v(-6.85, -2.66) * mm, "end": v(-9.5, -2.66) * mm});
            skLineSegment(sketch, "E76.MirrorCS", {"start": v(-6.85, -0.25) * mm, "end": v(-6.85, -2.66) * mm});
            skSolve(sketch);
        }
        {
            var Q0;
            Q0 = qSketchRegion(id + "F45", true);
            var Q1;
            {var subQ0=sQuery(id+"F5.wireOp",EDGE,"E28.top");var subQ8=sQuery(id+"F22.wireOp",EDGE,"E44.MirrorCS");var subQ11=sQuery(id+"F22.wireOp",EDGE,"E40");Q1=makeQuery(id+"F25.boolean.opBoolean","MERGE",FACE,{"derivedFrom":[makeQuery(id+"F23.boolean.opBoolean","COPY",FACE,{"disambiguationData":[TD([makeQuery(id+"F6.boolean.opBoolean","COPY",FACE,{"derivedFrom":makeQuery(id+"F6.opExtrude","SWEPT_FACE",FACE,{"disambiguationData":[OSD([subQ0])]})})])],"derivedFrom":makeQuery(id+"F23.opExtrude","CAP_FACE",FACE,{"disambiguationData":[OSD([subQ11,sQuery(id+"F22.wireOp",EDGE,"E41"),sQuery(id+"F22.wireOp",EDGE,"E42"),sQuery(id+"F22.wireOp",EDGE,"E43")])],"isStart":false})}),makeQuery(id+"F23.boolean.opBoolean","COPY",FACE,{"disambiguationData":[TD([makeQuery(id+"F9.boolean.opBoolean","COPY",FACE,{"derivedFrom":makeQuery(id+"F9.opExtrude","SWEPT_FACE",FACE,{"disambiguationData":[OSD([subQ0])]})})])],"derivedFrom":makeQuery(id+"F23.opExtrude","CAP_FACE",FACE,{"disambiguationData":[OSD([subQ8,sQuery(id+"F22.wireOp",EDGE,"E45.MirrorCS"),sQuery(id+"F22.wireOp",EDGE,"E46.MirrorCS"),sQuery(id+"F22.wireOp",EDGE,"E47.MirrorCS")])],"isStart":false})}),makeQuery(id+"F25.opExtrude","CAP_FACE",FACE,{"disambiguationData":[OSD([sQuery(id+"F24.wireOp",EDGE,"E50.bottom"),sQuery(id+"F24.wireOp",EDGE,"E50.top"),sQuery(id+"F24.wireOp",EDGE,"E50.left"),sQuery(id+"F24.wireOp",EDGE,"E50.right")])],"isStart":false})]});}
            extrude(context, id + "F46", {"entities" : qUnion([Q0]), "operationType" : NewBodyOperationType.REMOVE, "endBound" : BoundingType.UP_TO_SURFACE, "oppositeDirection" : true, "depth" : 25 * mm, "endBoundEntityFace" : qUnion([Q1]), "offsetDistance" : 25 * mm});
        }
    });
